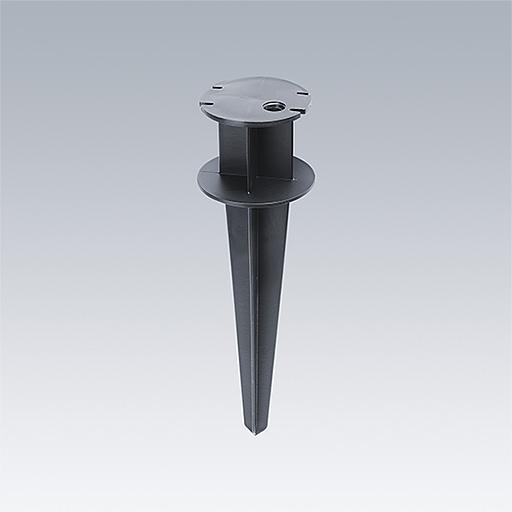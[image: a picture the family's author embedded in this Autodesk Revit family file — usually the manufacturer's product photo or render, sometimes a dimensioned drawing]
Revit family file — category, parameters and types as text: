
# Revit family: Thorn CESAR BOW
name_source: partatom
category: Lighting Fixtures
units: mm (PartAtom-declared; Revit-internal decimal feet)

## family parameters
Always vertical = No
Cut with Voids When Loaded = Yes
Light Source = Yes
Maintain Annotation Orientation = No
Part Type = Normal
Room Calculation Point = Yes
Round Connector Dimension = Use Diameter
Shared = No
Work Plane-Based = No

## types (96) — shared parameters
Assembly Code = Pr_70_70_48_62
Color Filter = 16777215
Description = Ground Surface Mounted Luminaire
Dimming Lamp Color Temperature Shift = <None>
Export Type to IFC As = IfcLightFixtureType
Ground Spike = No
Lamp = LED
Manufacturer = Thorn Lighting
Power Factor = 0.97
SELECT ACCESSORIES = SELECT ACCESSORIES
SELECT HOUSING = SELECT HOUSING
SELECT LIGHT DISTRIBUTION = SELECT LIGHT DISTRIBUTION
Tilt Angle = 90.00°
Type IFC Predefined Type = DIRECTIONSOURCE
URL = https://www.thornlighting.com
zero-valued in all types: Default Elevation, H

## per-type parameters (varying)
| type | Apparent Load | Beam Assymetric | Beam Medium | Beam Narrow | Beam Wide | Inner Circle Diameter | Inner Circle Radius | Luminaire Diameter | Luminaire Height | Luminaire Length | Luminaire Radius | Luminaire Width | Material Housing | Model | Photometric Web File | Size Medium | Size Small | Type Image |
| CESAR BOW S 4L 927 NB RD ANT | 8 VA | No | No | Yes | No | 46.5 mm  [stored 0.152559 ft] | 93 mm  [stored 0.305118 ft] | 100 mm  [stored 0.328084 ft] | 29 mm  [stored 0.0951444 ft] | 200 mm  [stored 0.656168 ft] | 200 mm  [stored 0.656168 ft] | 200 mm  [stored 0.656168 ft] | Thorn-Aluminium-RAL 7016-Anthracite Grey | 96800712 | 96800712_(STD).IES | No | Yes | TLG_CESA_F_BOW_S_ANT.jpg |
| CESAR BOW S 4L 927 NB RD BK | 8 VA | No | No | Yes | No | 46.5 mm  [stored 0.152559 ft] | 93 mm  [stored 0.305118 ft] | 100 mm  [stored 0.328084 ft] | 29 mm  [stored 0.0951444 ft] | 200 mm  [stored 0.656168 ft] | 200 mm  [stored 0.656168 ft] | 200 mm  [stored 0.656168 ft] | Thorn-Aluminium-RAL 9005-Jet Black | 96800710 | 96800710_(STD).IES | No | Yes | TLG_CESA_F_BOW_S_BK.jpg |
| CESAR BOW S 4L 927 NB RD GY | 8 VA | No | No | Yes | No | 46.5 mm  [stored 0.152559 ft] | 93 mm  [stored 0.305118 ft] | 100 mm  [stored 0.328084 ft] | 29 mm  [stored 0.0951444 ft] | 200 mm  [stored 0.656168 ft] | 200 mm  [stored 0.656168 ft] | 200 mm  [stored 0.656168 ft] | Thorn-Aluminium-RAL 9006-White Aluminium | 96800711 | 96800711_(STD).IES | No | Yes | TLG_CESA_F_BOW_S_GY.jpg |
| CESAR BOW S 4L 927 NB RD WH | 8 VA | No | No | Yes | No | 46.5 mm  [stored 0.152559 ft] | 93 mm  [stored 0.305118 ft] | 100 mm  [stored 0.328084 ft] | 29 mm  [stored 0.0951444 ft] | 200 mm  [stored 0.656168 ft] | 200 mm  [stored 0.656168 ft] | 200 mm  [stored 0.656168 ft] | Thorn-Aluminium-RAL 9016-Traffic White | 96800709 | 96800709_(STD).IES | No | Yes | TLG_CESA_F_BOW_S_WH.jpg |
| CESAR BOW S 4L 930 NB RD ANT | 8 VA | No | No | Yes | No | 46.5 mm  [stored 0.152559 ft] | 93 mm  [stored 0.305118 ft] | 100 mm  [stored 0.328084 ft] | 29 mm  [stored 0.0951444 ft] | 200 mm  [stored 0.656168 ft] | 200 mm  [stored 0.656168 ft] | 200 mm  [stored 0.656168 ft] | Thorn-Aluminium-RAL 7016-Anthracite Grey | 96800720 | 96800720_(STD).IES | No | Yes | TLG_CESA_F_BOW_S_ANT.jpg |
| CESAR BOW S 4L 930 NB RD BK | 8 VA | No | No | Yes | No | 46.5 mm  [stored 0.152559 ft] | 93 mm  [stored 0.305118 ft] | 100 mm  [stored 0.328084 ft] | 29 mm  [stored 0.0951444 ft] | 200 mm  [stored 0.656168 ft] | 200 mm  [stored 0.656168 ft] | 200 mm  [stored 0.656168 ft] | Thorn-Aluminium-RAL 9005-Jet Black | 96800718 | 96800718_(STD).IES | No | Yes | TLG_CESA_F_BOW_S_BK.jpg |
| CESAR BOW S 4L 930 NB RD GY | 8 VA | No | No | Yes | No | 46.5 mm  [stored 0.152559 ft] | 93 mm  [stored 0.305118 ft] | 100 mm  [stored 0.328084 ft] | 29 mm  [stored 0.0951444 ft] | 200 mm  [stored 0.656168 ft] | 200 mm  [stored 0.656168 ft] | 200 mm  [stored 0.656168 ft] | Thorn-Aluminium-RAL 9006-White Aluminium | 96800719 | 96800719_(STD).IES | No | Yes | TLG_CESA_F_BOW_S_GY.jpg |
| CESAR BOW S 4L 930 NB RD WH | 8 VA | No | No | Yes | No | 46.5 mm  [stored 0.152559 ft] | 93 mm  [stored 0.305118 ft] | 100 mm  [stored 0.328084 ft] | 29 mm  [stored 0.0951444 ft] | 200 mm  [stored 0.656168 ft] | 200 mm  [stored 0.656168 ft] | 200 mm  [stored 0.656168 ft] | Thorn-Aluminium-RAL 9016-Traffic White | 96800717 | 96800717_(STD).IES | No | Yes | TLG_CESA_F_BOW_S_WH.jpg |
| CESAR BOW S 4L 940 NB RD ANT | 8 VA | No | No | Yes | No | 46.5 mm  [stored 0.152559 ft] | 93 mm  [stored 0.305118 ft] | 100 mm  [stored 0.328084 ft] | 29 mm  [stored 0.0951444 ft] | 200 mm  [stored 0.656168 ft] | 200 mm  [stored 0.656168 ft] | 200 mm  [stored 0.656168 ft] | Thorn-Aluminium-RAL 7016-Anthracite Grey | 96800716 | 96800716_(STD).IES | No | Yes | TLG_CESA_F_BOW_S_ANT.jpg |
| CESAR BOW S 4L 940 NB RD BK | 8 VA | No | No | Yes | No | 46.5 mm  [stored 0.152559 ft] | 93 mm  [stored 0.305118 ft] | 100 mm  [stored 0.328084 ft] | 29 mm  [stored 0.0951444 ft] | 200 mm  [stored 0.656168 ft] | 200 mm  [stored 0.656168 ft] | 200 mm  [stored 0.656168 ft] | Thorn-Aluminium-RAL 9005-Jet Black | 96800714 | 96800714_(STD).IES | No | Yes | TLG_CESA_F_BOW_S_BK.jpg |
| CESAR BOW S 4L 940 NB RD GY | 8 VA | No | No | Yes | No | 46.5 mm  [stored 0.152559 ft] | 93 mm  [stored 0.305118 ft] | 100 mm  [stored 0.328084 ft] | 29 mm  [stored 0.0951444 ft] | 200 mm  [stored 0.656168 ft] | 200 mm  [stored 0.656168 ft] | 200 mm  [stored 0.656168 ft] | Thorn-Aluminium-RAL 9006-White Aluminium | 96800715 | 96800715_(STD).IES | No | Yes | TLG_CESA_F_BOW_S_GY.jpg |
| CESAR BOW S 4L 940 NB RD WH | 8 VA | No | No | Yes | No | 46.5 mm  [stored 0.152559 ft] | 93 mm  [stored 0.305118 ft] | 100 mm  [stored 0.328084 ft] | 29 mm  [stored 0.0951444 ft] | 200 mm  [stored 0.656168 ft] | 200 mm  [stored 0.656168 ft] | 200 mm  [stored 0.656168 ft] | Thorn-Aluminium-RAL 9016-Traffic White | 96800713 | 96800713_(STD).IES | No | Yes | TLG_CESA_F_BOW_S_WH.jpg |
| CESAR BOW S 4L 927 MB RD ANT | 8 VA | No | Yes | No | No | 46.5 mm  [stored 0.152559 ft] | 93 mm  [stored 0.305118 ft] | 100 mm  [stored 0.328084 ft] | 29 mm  [stored 0.0951444 ft] | 200 mm  [stored 0.656168 ft] | 200 mm  [stored 0.656168 ft] | 200 mm  [stored 0.656168 ft] | Thorn-Aluminium-RAL 7016-Anthracite Grey | 96800724 | 96800724_(STD).IES | No | Yes | TLG_CESA_F_BOW_S_ANT.jpg |
| CESAR BOW S 4L 927 MB RD BK | 8 VA | No | Yes | No | No | 46.5 mm  [stored 0.152559 ft] | 93 mm  [stored 0.305118 ft] | 100 mm  [stored 0.328084 ft] | 29 mm  [stored 0.0951444 ft] | 200 mm  [stored 0.656168 ft] | 200 mm  [stored 0.656168 ft] | 200 mm  [stored 0.656168 ft] | Thorn-Aluminium-RAL 9005-Jet Black | 96800722 | 96800722_(STD).IES | No | Yes | TLG_CESA_F_BOW_S_BK.jpg |
| CESAR BOW S 4L 927 MB RD GY | 8 VA | No | Yes | No | No | 46.5 mm  [stored 0.152559 ft] | 93 mm  [stored 0.305118 ft] | 100 mm  [stored 0.328084 ft] | 29 mm  [stored 0.0951444 ft] | 200 mm  [stored 0.656168 ft] | 200 mm  [stored 0.656168 ft] | 200 mm  [stored 0.656168 ft] | Thorn-Aluminium-RAL 9006-White Aluminium | 96800723 | 96800723_(STD).IES | No | Yes | TLG_CESA_F_BOW_S_GY.jpg |
| CESAR BOW S 4L 927 MB RD WH | 8 VA | No | Yes | No | No | 46.5 mm  [stored 0.152559 ft] | 93 mm  [stored 0.305118 ft] | 100 mm  [stored 0.328084 ft] | 29 mm  [stored 0.0951444 ft] | 200 mm  [stored 0.656168 ft] | 200 mm  [stored 0.656168 ft] | 200 mm  [stored 0.656168 ft] | Thorn-Aluminium-RAL 9016-Traffic White | 96800721 | 96800721_(STD).IES | No | Yes | TLG_CESA_F_BOW_S_WH.jpg |
| CESAR BOW S 4L 930 MB RD ANT | 8 VA | No | Yes | No | No | 46.5 mm  [stored 0.152559 ft] | 93 mm  [stored 0.305118 ft] | 100 mm  [stored 0.328084 ft] | 29 mm  [stored 0.0951444 ft] | 200 mm  [stored 0.656168 ft] | 200 mm  [stored 0.656168 ft] | 200 mm  [stored 0.656168 ft] | Thorn-Aluminium-RAL 7016-Anthracite Grey | 96800732 | 96800732_(STD).IES | No | Yes | TLG_CESA_F_BOW_S_ANT.jpg |
| CESAR BOW S 4L 930 MB RD BK | 8 VA | No | Yes | No | No | 46.5 mm  [stored 0.152559 ft] | 93 mm  [stored 0.305118 ft] | 100 mm  [stored 0.328084 ft] | 29 mm  [stored 0.0951444 ft] | 200 mm  [stored 0.656168 ft] | 200 mm  [stored 0.656168 ft] | 200 mm  [stored 0.656168 ft] | Thorn-Aluminium-RAL 9005-Jet Black | 96800730 | 96800730_(STD).IES | No | Yes | TLG_CESA_F_BOW_S_BK.jpg |
| CESAR BOW S 4L 930 MB RD GY | 8 VA | No | Yes | No | No | 46.5 mm  [stored 0.152559 ft] | 93 mm  [stored 0.305118 ft] | 100 mm  [stored 0.328084 ft] | 29 mm  [stored 0.0951444 ft] | 200 mm  [stored 0.656168 ft] | 200 mm  [stored 0.656168 ft] | 200 mm  [stored 0.656168 ft] | Thorn-Aluminium-RAL 9006-White Aluminium | 96800731 | 96800731_(STD).IES | No | Yes | TLG_CESA_F_BOW_S_GY.jpg |
| CESAR BOW S 4L 930 MB RD WH | 8 VA | No | Yes | No | No | 46.5 mm  [stored 0.152559 ft] | 93 mm  [stored 0.305118 ft] | 100 mm  [stored 0.328084 ft] | 29 mm  [stored 0.0951444 ft] | 200 mm  [stored 0.656168 ft] | 200 mm  [stored 0.656168 ft] | 200 mm  [stored 0.656168 ft] | Thorn-Aluminium-RAL 9016-Traffic White | 96800729 | 96800729_(STD).IES | No | Yes | TLG_CESA_F_BOW_S_WH.jpg |
| CESAR BOW S 4L 940 MB RD ANT | 8 VA | No | Yes | No | No | 46.5 mm  [stored 0.152559 ft] | 93 mm  [stored 0.305118 ft] | 100 mm  [stored 0.328084 ft] | 29 mm  [stored 0.0951444 ft] | 200 mm  [stored 0.656168 ft] | 200 mm  [stored 0.656168 ft] | 200 mm  [stored 0.656168 ft] | Thorn-Aluminium-RAL 7016-Anthracite Grey | 96800728 | 96800728_(STD).IES | No | Yes | TLG_CESA_F_BOW_S_ANT.jpg |
| CESAR BOW S 4L 940 MB RD BK | 8 VA | No | Yes | No | No | 46.5 mm  [stored 0.152559 ft] | 93 mm  [stored 0.305118 ft] | 100 mm  [stored 0.328084 ft] | 29 mm  [stored 0.0951444 ft] | 200 mm  [stored 0.656168 ft] | 200 mm  [stored 0.656168 ft] | 200 mm  [stored 0.656168 ft] | Thorn-Aluminium-RAL 9005-Jet Black | 96800726 | 96800726_(STD).IES | No | Yes | TLG_CESA_F_BOW_S_BK.jpg |
| CESAR BOW S 4L 940 MB RD GY | 8 VA | No | Yes | No | No | 46.5 mm  [stored 0.152559 ft] | 93 mm  [stored 0.305118 ft] | 100 mm  [stored 0.328084 ft] | 29 mm  [stored 0.0951444 ft] | 200 mm  [stored 0.656168 ft] | 200 mm  [stored 0.656168 ft] | 200 mm  [stored 0.656168 ft] | Thorn-Aluminium-RAL 9006-White Aluminium | 96800727 | 96800727_(STD).IES | No | Yes | TLG_CESA_F_BOW_S_GY.jpg |
| CESAR BOW S 4L 940 MB RD WH | 8 VA | No | Yes | No | No | 46.5 mm  [stored 0.152559 ft] | 93 mm  [stored 0.305118 ft] | 100 mm  [stored 0.328084 ft] | 29 mm  [stored 0.0951444 ft] | 200 mm  [stored 0.656168 ft] | 200 mm  [stored 0.656168 ft] | 200 mm  [stored 0.656168 ft] | Thorn-Aluminium-RAL 9016-Traffic White | 96800725 | 96800725_(STD).IES | No | Yes | TLG_CESA_F_BOW_S_WH.jpg |
| CESAR BOW S 4L 927 WB RD ANT | 8 VA | No | No | No | Yes | 46.5 mm  [stored 0.152559 ft] | 93 mm  [stored 0.305118 ft] | 100 mm  [stored 0.328084 ft] | 29 mm  [stored 0.0951444 ft] | 200 mm  [stored 0.656168 ft] | 200 mm  [stored 0.656168 ft] | 200 mm  [stored 0.656168 ft] | Thorn-Aluminium-RAL 7016-Anthracite Grey | 96800736 | 96800736_(STD).IES | No | Yes | TLG_CESA_F_BOW_S_ANT.jpg |
| CESAR BOW S 4L 927 WB RD BK | 8 VA | No | No | No | Yes | 46.5 mm  [stored 0.152559 ft] | 93 mm  [stored 0.305118 ft] | 100 mm  [stored 0.328084 ft] | 29 mm  [stored 0.0951444 ft] | 200 mm  [stored 0.656168 ft] | 200 mm  [stored 0.656168 ft] | 200 mm  [stored 0.656168 ft] | Thorn-Aluminium-RAL 9005-Jet Black | 96800734 | 96800734_(STD).IES | No | Yes | TLG_CESA_F_BOW_S_BK.jpg |
| CESAR BOW S 4L 927 WB RD GY | 8 VA | No | No | No | Yes | 46.5 mm  [stored 0.152559 ft] | 93 mm  [stored 0.305118 ft] | 100 mm  [stored 0.328084 ft] | 29 mm  [stored 0.0951444 ft] | 200 mm  [stored 0.656168 ft] | 200 mm  [stored 0.656168 ft] | 200 mm  [stored 0.656168 ft] | Thorn-Aluminium-RAL 9006-White Aluminium | 96800735 | 96800735_(STD).IES | No | Yes | TLG_CESA_F_BOW_S_GY.jpg |
| CESAR BOW S 4L 927 WB RD WH | 8 VA | No | No | No | Yes | 46.5 mm  [stored 0.152559 ft] | 93 mm  [stored 0.305118 ft] | 100 mm  [stored 0.328084 ft] | 29 mm  [stored 0.0951444 ft] | 200 mm  [stored 0.656168 ft] | 200 mm  [stored 0.656168 ft] | 200 mm  [stored 0.656168 ft] | Thorn-Aluminium-RAL 9016-Traffic White | 96800733 | 96800733_(STD).IES | No | Yes | TLG_CESA_F_BOW_S_WH.jpg |
| CESAR BOW S 4L 930 WB RD ANT | 8 VA | No | No | No | Yes | 46.5 mm  [stored 0.152559 ft] | 93 mm  [stored 0.305118 ft] | 100 mm  [stored 0.328084 ft] | 29 mm  [stored 0.0951444 ft] | 200 mm  [stored 0.656168 ft] | 200 mm  [stored 0.656168 ft] | 200 mm  [stored 0.656168 ft] | Thorn-Aluminium-RAL 7016-Anthracite Grey | 96800744 | 96800744_(STD).IES | No | Yes | TLG_CESA_F_BOW_S_ANT.jpg |
| CESAR BOW S 4L 930 WB RD BK | 8 VA | No | No | No | Yes | 46.5 mm  [stored 0.152559 ft] | 93 mm  [stored 0.305118 ft] | 100 mm  [stored 0.328084 ft] | 29 mm  [stored 0.0951444 ft] | 200 mm  [stored 0.656168 ft] | 200 mm  [stored 0.656168 ft] | 200 mm  [stored 0.656168 ft] | Thorn-Aluminium-RAL 9005-Jet Black | 96800742 | 96800742_(STD).IES | No | Yes | TLG_CESA_F_BOW_S_BK.jpg |
| CESAR BOW S 4L 930 WB RD GY | 8 VA | No | No | No | Yes | 46.5 mm  [stored 0.152559 ft] | 93 mm  [stored 0.305118 ft] | 100 mm  [stored 0.328084 ft] | 29 mm  [stored 0.0951444 ft] | 200 mm  [stored 0.656168 ft] | 200 mm  [stored 0.656168 ft] | 200 mm  [stored 0.656168 ft] | Thorn-Aluminium-RAL 9006-White Aluminium | 96800743 | 96800743_(STD).IES | No | Yes | TLG_CESA_F_BOW_S_GY.jpg |
| CESAR BOW S 4L 930 WB RD WH | 8 VA | No | No | No | Yes | 46.5 mm  [stored 0.152559 ft] | 93 mm  [stored 0.305118 ft] | 100 mm  [stored 0.328084 ft] | 29 mm  [stored 0.0951444 ft] | 200 mm  [stored 0.656168 ft] | 200 mm  [stored 0.656168 ft] | 200 mm  [stored 0.656168 ft] | Thorn-Aluminium-RAL 9016-Traffic White | 96800741 | 96800741_(STD).IES | No | Yes | TLG_CESA_F_BOW_S_WH.jpg |
| CESAR BOW S 4L 940 WB RD ANT | 8 VA | No | No | No | Yes | 46.5 mm  [stored 0.152559 ft] | 93 mm  [stored 0.305118 ft] | 100 mm  [stored 0.328084 ft] | 29 mm  [stored 0.0951444 ft] | 200 mm  [stored 0.656168 ft] | 200 mm  [stored 0.656168 ft] | 200 mm  [stored 0.656168 ft] | Thorn-Aluminium-RAL 7016-Anthracite Grey | 96800740 | 96800740_(STD).IES | No | Yes | TLG_CESA_F_BOW_S_ANT.jpg |
| CESAR BOW S 4L 940 WB RD BK | 8 VA | No | No | No | Yes | 46.5 mm  [stored 0.152559 ft] | 93 mm  [stored 0.305118 ft] | 100 mm  [stored 0.328084 ft] | 29 mm  [stored 0.0951444 ft] | 200 mm  [stored 0.656168 ft] | 200 mm  [stored 0.656168 ft] | 200 mm  [stored 0.656168 ft] | Thorn-Aluminium-RAL 9005-Jet Black | 96800738 | 96800738_(STD).IES | No | Yes | TLG_CESA_F_BOW_S_BK.jpg |
| CESAR BOW S 4L 940 WB RD GY | 8 VA | No | No | No | Yes | 46.5 mm  [stored 0.152559 ft] | 93 mm  [stored 0.305118 ft] | 100 mm  [stored 0.328084 ft] | 29 mm  [stored 0.0951444 ft] | 200 mm  [stored 0.656168 ft] | 200 mm  [stored 0.656168 ft] | 200 mm  [stored 0.656168 ft] | Thorn-Aluminium-RAL 9006-White Aluminium | 96800739 | 96800739_(STD).IES | No | Yes | TLG_CESA_F_BOW_S_GY.jpg |
| CESAR BOW S 4L 940 WB RD WH | 8 VA | No | No | No | Yes | 46.5 mm  [stored 0.152559 ft] | 93 mm  [stored 0.305118 ft] | 100 mm  [stored 0.328084 ft] | 29 mm  [stored 0.0951444 ft] | 200 mm  [stored 0.656168 ft] | 200 mm  [stored 0.656168 ft] | 200 mm  [stored 0.656168 ft] | Thorn-Aluminium-RAL 9016-Traffic White | 96800737 | 96800737_(STD).IES | No | Yes | TLG_CESA_F_BOW_S_WH.jpg |
| CESAR BOW S 4L 927 AS RD ANT | 8 VA | Yes | No | No | No | 46.5 mm  [stored 0.152559 ft] | 93 mm  [stored 0.305118 ft] | 100 mm  [stored 0.328084 ft] | 29 mm  [stored 0.0951444 ft] | 200 mm  [stored 0.656168 ft] | 200 mm  [stored 0.656168 ft] | 200 mm  [stored 0.656168 ft] | Thorn-Aluminium-RAL 7016-Anthracite Grey | 96800748 | 96800748_(STD).IES | No | Yes | TLG_CESA_F_BOW_S_ANT.jpg |
| CESAR BOW S 4L 927 AS RD BK | 8 VA | Yes | No | No | No | 46.5 mm  [stored 0.152559 ft] | 93 mm  [stored 0.305118 ft] | 100 mm  [stored 0.328084 ft] | 29 mm  [stored 0.0951444 ft] | 200 mm  [stored 0.656168 ft] | 200 mm  [stored 0.656168 ft] | 200 mm  [stored 0.656168 ft] | Thorn-Aluminium-RAL 9005-Jet Black | 96800746 | 96800746_(STD).IES | No | Yes | TLG_CESA_F_BOW_S_BK.jpg |
| CESAR BOW S 4L 927 AS RD GY | 8 VA | Yes | No | No | No | 46.5 mm  [stored 0.152559 ft] | 93 mm  [stored 0.305118 ft] | 100 mm  [stored 0.328084 ft] | 29 mm  [stored 0.0951444 ft] | 200 mm  [stored 0.656168 ft] | 200 mm  [stored 0.656168 ft] | 200 mm  [stored 0.656168 ft] | Thorn-Aluminium-RAL 9006-White Aluminium | 96800747 | 96800747_(STD).IES | No | Yes | TLG_CESA_F_BOW_S_GY.jpg |
| CESAR BOW S 4L 927 AS RD WH | 8 VA | Yes | No | No | No | 46.5 mm  [stored 0.152559 ft] | 93 mm  [stored 0.305118 ft] | 100 mm  [stored 0.328084 ft] | 29 mm  [stored 0.0951444 ft] | 200 mm  [stored 0.656168 ft] | 200 mm  [stored 0.656168 ft] | 200 mm  [stored 0.656168 ft] | Thorn-Aluminium-RAL 9016-Traffic White | 96800745 | 96800745_(STD).IES | No | Yes | TLG_CESA_F_BOW_S_WH.jpg |
| CESAR BOW S 4L 930 AS RD ANT | 8 VA | Yes | No | No | No | 46.5 mm  [stored 0.152559 ft] | 93 mm  [stored 0.305118 ft] | 100 mm  [stored 0.328084 ft] | 29 mm  [stored 0.0951444 ft] | 200 mm  [stored 0.656168 ft] | 200 mm  [stored 0.656168 ft] | 200 mm  [stored 0.656168 ft] | Thorn-Aluminium-RAL 7016-Anthracite Grey | 96800756 | 96800756_(STD).IES | No | Yes | TLG_CESA_F_BOW_S_ANT.jpg |
| CESAR BOW S 4L 930 AS RD BK | 8 VA | Yes | No | No | No | 46.5 mm  [stored 0.152559 ft] | 93 mm  [stored 0.305118 ft] | 100 mm  [stored 0.328084 ft] | 29 mm  [stored 0.0951444 ft] | 200 mm  [stored 0.656168 ft] | 200 mm  [stored 0.656168 ft] | 200 mm  [stored 0.656168 ft] | Thorn-Aluminium-RAL 9005-Jet Black | 96800754 | 96800754_(STD).IES | No | Yes | TLG_CESA_F_BOW_S_BK.jpg |
| CESAR BOW S 4L 930 AS RD GY | 8 VA | Yes | No | No | No | 46.5 mm  [stored 0.152559 ft] | 93 mm  [stored 0.305118 ft] | 100 mm  [stored 0.328084 ft] | 29 mm  [stored 0.0951444 ft] | 200 mm  [stored 0.656168 ft] | 200 mm  [stored 0.656168 ft] | 200 mm  [stored 0.656168 ft] | Thorn-Aluminium-RAL 9006-White Aluminium | 96800755 | 96800755_(STD).IES | No | Yes | TLG_CESA_F_BOW_S_GY.jpg |
| CESAR BOW S 4L 930 AS RD WH | 8 VA | Yes | No | No | No | 46.5 mm  [stored 0.152559 ft] | 93 mm  [stored 0.305118 ft] | 100 mm  [stored 0.328084 ft] | 29 mm  [stored 0.0951444 ft] | 200 mm  [stored 0.656168 ft] | 200 mm  [stored 0.656168 ft] | 200 mm  [stored 0.656168 ft] | Thorn-Aluminium-RAL 9016-Traffic White | 96800753 | 96800753_(STD).IES | No | Yes | TLG_CESA_F_BOW_S_WH.jpg |
| CESAR BOW S 4L 940 AS RD ANT | 8 VA | Yes | No | No | No | 46.5 mm  [stored 0.152559 ft] | 93 mm  [stored 0.305118 ft] | 100 mm  [stored 0.328084 ft] | 29 mm  [stored 0.0951444 ft] | 200 mm  [stored 0.656168 ft] | 200 mm  [stored 0.656168 ft] | 200 mm  [stored 0.656168 ft] | Thorn-Aluminium-RAL 7016-Anthracite Grey | 96800752 | 96800752_(STD).IES | No | Yes | TLG_CESA_F_BOW_S_ANT.jpg |
| CESAR BOW S 4L 940 AS RD BK | 8 VA | Yes | No | No | No | 46.5 mm  [stored 0.152559 ft] | 93 mm  [stored 0.305118 ft] | 100 mm  [stored 0.328084 ft] | 29 mm  [stored 0.0951444 ft] | 200 mm  [stored 0.656168 ft] | 200 mm  [stored 0.656168 ft] | 200 mm  [stored 0.656168 ft] | Thorn-Aluminium-RAL 9005-Jet Black | 96800750 | 96800750_(STD).IES | No | Yes | TLG_CESA_F_BOW_S_BK.jpg |
| CESAR BOW S 4L 940 AS RD GY | 8 VA | Yes | No | No | No | 46.5 mm  [stored 0.152559 ft] | 93 mm  [stored 0.305118 ft] | 100 mm  [stored 0.328084 ft] | 29 mm  [stored 0.0951444 ft] | 200 mm  [stored 0.656168 ft] | 200 mm  [stored 0.656168 ft] | 200 mm  [stored 0.656168 ft] | Thorn-Aluminium-RAL 9006-White Aluminium | 96800751 | 96800751_(STD).IES | No | Yes | TLG_CESA_F_BOW_S_GY.jpg |
| CESAR BOW S 4L 940 AS RD WH | 8 VA | Yes | No | No | No | 46.5 mm  [stored 0.152559 ft] | 93 mm  [stored 0.305118 ft] | 100 mm  [stored 0.328084 ft] | 29 mm  [stored 0.0951444 ft] | 200 mm  [stored 0.656168 ft] | 200 mm  [stored 0.656168 ft] | 200 mm  [stored 0.656168 ft] | Thorn-Aluminium-RAL 9016-Traffic White | 96800749 | 96800749_(STD).IES | No | Yes | TLG_CESA_F_BOW_S_WH.jpg |
| CESAR BOW M 9L 927 NB RD ANT | 19 VA | No | No | Yes | No | 69 mm  [stored 0.226378 ft] | 138 mm  [stored 0.452756 ft] | 130 mm  [stored 0.426509 ft] | 31 mm  [stored 0.101706 ft] | 260 mm  [stored 0.853018 ft] | 260 mm  [stored 0.853018 ft] | 260 mm  [stored 0.853018 ft] | Thorn-Aluminium-RAL 7016-Anthracite Grey | 96800760 | 96800760_(STD).IES | Yes | No | TLG_CESA_F_BOW_M_9L_ANT.jpg |
| CESAR BOW M 9L 927 NB RD BK | 19 VA | No | No | Yes | No | 69 mm  [stored 0.226378 ft] | 138 mm  [stored 0.452756 ft] | 130 mm  [stored 0.426509 ft] | 31 mm  [stored 0.101706 ft] | 260 mm  [stored 0.853018 ft] | 260 mm  [stored 0.853018 ft] | 260 mm  [stored 0.853018 ft] | Thorn-Aluminium-RAL 9005-Jet Black | 96800758 | 96800758_(STD).IES | Yes | No | TLG_CESA_F_BOW_M_9L_BK.jpg |
| CESAR BOW M 9L 927 NB RD GY | 19 VA | No | No | Yes | No | 69 mm  [stored 0.226378 ft] | 138 mm  [stored 0.452756 ft] | 130 mm  [stored 0.426509 ft] | 31 mm  [stored 0.101706 ft] | 260 mm  [stored 0.853018 ft] | 260 mm  [stored 0.853018 ft] | 260 mm  [stored 0.853018 ft] | Thorn-Aluminium-RAL 9006-White Aluminium | 96800759 | 96800759_(STD).IES | Yes | No | TLG_CESA_F_BOW_M_9L_GY.jpg |
| CESAR BOW M 9L 927 NB RD WH | 19 VA | No | No | Yes | No | 69 mm  [stored 0.226378 ft] | 138 mm  [stored 0.452756 ft] | 130 mm  [stored 0.426509 ft] | 31 mm  [stored 0.101706 ft] | 260 mm  [stored 0.853018 ft] | 260 mm  [stored 0.853018 ft] | 260 mm  [stored 0.853018 ft] | Thorn-Aluminium-RAL 9016-Traffic White | 96800757 | 96800757_(STD).IES | Yes | No | TLG_CESA_F_BOW_M_9L_WH.jpg |
| CESAR BOW M 9L 930 NB RD ANT | 19 VA | No | No | Yes | No | 69 mm  [stored 0.226378 ft] | 138 mm  [stored 0.452756 ft] | 130 mm  [stored 0.426509 ft] | 31 mm  [stored 0.101706 ft] | 260 mm  [stored 0.853018 ft] | 260 mm  [stored 0.853018 ft] | 260 mm  [stored 0.853018 ft] | Thorn-Aluminium-RAL 7016-Anthracite Grey | 96800768 | 96800768_(STD).IES | Yes | No | TLG_CESA_F_BOW_M_9L_ANT.jpg |
| CESAR BOW M 9L 930 NB RD BK | 19 VA | No | No | Yes | No | 69 mm  [stored 0.226378 ft] | 138 mm  [stored 0.452756 ft] | 130 mm  [stored 0.426509 ft] | 31 mm  [stored 0.101706 ft] | 260 mm  [stored 0.853018 ft] | 260 mm  [stored 0.853018 ft] | 260 mm  [stored 0.853018 ft] | Thorn-Aluminium-RAL 9005-Jet Black | 96800766 | 96800766_(STD).IES | Yes | No | TLG_CESA_F_BOW_M_9L_BK.jpg |
| CESAR BOW M 9L 930 NB RD GY | 19 VA | No | No | Yes | No | 69 mm  [stored 0.226378 ft] | 138 mm  [stored 0.452756 ft] | 130 mm  [stored 0.426509 ft] | 31 mm  [stored 0.101706 ft] | 260 mm  [stored 0.853018 ft] | 260 mm  [stored 0.853018 ft] | 260 mm  [stored 0.853018 ft] | Thorn-Aluminium-RAL 9006-White Aluminium | 96800767 | 96800767_(STD).IES | Yes | No | TLG_CESA_F_BOW_M_9L_GY.jpg |
| CESAR BOW M 9L 930 NB RD WH | 19 VA | No | No | Yes | No | 69 mm  [stored 0.226378 ft] | 138 mm  [stored 0.452756 ft] | 130 mm  [stored 0.426509 ft] | 31 mm  [stored 0.101706 ft] | 260 mm  [stored 0.853018 ft] | 260 mm  [stored 0.853018 ft] | 260 mm  [stored 0.853018 ft] | Thorn-Aluminium-RAL 9016-Traffic White | 96800765 | 96800765_(STD).IES | Yes | No | TLG_CESA_F_BOW_M_9L_WH.jpg |
| CESAR BOW M 9L 940 NB RD ANT | 19 VA | No | No | Yes | No | 69 mm  [stored 0.226378 ft] | 138 mm  [stored 0.452756 ft] | 130 mm  [stored 0.426509 ft] | 31 mm  [stored 0.101706 ft] | 260 mm  [stored 0.853018 ft] | 260 mm  [stored 0.853018 ft] | 260 mm  [stored 0.853018 ft] | Thorn-Aluminium-RAL 7016-Anthracite Grey | 96800764 | 96800764_(STD).IES | Yes | No | TLG_CESA_F_BOW_M_9L_ANT.jpg |
| CESAR BOW M 9L 940 NB RD BK | 19 VA | No | No | Yes | No | 69 mm  [stored 0.226378 ft] | 138 mm  [stored 0.452756 ft] | 130 mm  [stored 0.426509 ft] | 31 mm  [stored 0.101706 ft] | 260 mm  [stored 0.853018 ft] | 260 mm  [stored 0.853018 ft] | 260 mm  [stored 0.853018 ft] | Thorn-Aluminium-RAL 9005-Jet Black | 96800762 | 96800762_(STD).IES | Yes | No | TLG_CESA_F_BOW_M_9L_BK.jpg |
| CESAR BOW M 9L 940 NB RD GY | 19 VA | No | No | Yes | No | 69 mm  [stored 0.226378 ft] | 138 mm  [stored 0.452756 ft] | 130 mm  [stored 0.426509 ft] | 31 mm  [stored 0.101706 ft] | 260 mm  [stored 0.853018 ft] | 260 mm  [stored 0.853018 ft] | 260 mm  [stored 0.853018 ft] | Thorn-Aluminium-RAL 9006-White Aluminium | 96800763 | 96800763_(STD).IES | Yes | No | TLG_CESA_F_BOW_M_9L_GY.jpg |
| CESAR BOW M 9L 940 NB RD WH | 19 VA | No | No | Yes | No | 69 mm  [stored 0.226378 ft] | 138 mm  [stored 0.452756 ft] | 130 mm  [stored 0.426509 ft] | 31 mm  [stored 0.101706 ft] | 260 mm  [stored 0.853018 ft] | 260 mm  [stored 0.853018 ft] | 260 mm  [stored 0.853018 ft] | Thorn-Aluminium-RAL 9016-Traffic White | 96800761 | 96800761_(STD).IES | Yes | No | TLG_CESA_F_BOW_M_9L_WH.jpg |
| CESAR BOW M 9L 927 MB RD ANT | 19 VA | No | Yes | No | No | 69 mm  [stored 0.226378 ft] | 138 mm  [stored 0.452756 ft] | 130 mm  [stored 0.426509 ft] | 31 mm  [stored 0.101706 ft] | 260 mm  [stored 0.853018 ft] | 260 mm  [stored 0.853018 ft] | 260 mm  [stored 0.853018 ft] | Thorn-Aluminium-RAL 7016-Anthracite Grey | 96800772 | 96800772_(STD).IES | Yes | No | TLG_CESA_F_BOW_M_9L_ANT.jpg |
| CESAR BOW M 9L 927 MB RD BK | 19 VA | No | Yes | No | No | 69 mm  [stored 0.226378 ft] | 138 mm  [stored 0.452756 ft] | 130 mm  [stored 0.426509 ft] | 31 mm  [stored 0.101706 ft] | 260 mm  [stored 0.853018 ft] | 260 mm  [stored 0.853018 ft] | 260 mm  [stored 0.853018 ft] | Thorn-Aluminium-RAL 9005-Jet Black | 96800770 | 96800770_(STD).IES | Yes | No | TLG_CESA_F_BOW_M_9L_BK.jpg |
| CESAR BOW M 9L 927 MB RD GY | 19 VA | No | Yes | No | No | 69 mm  [stored 0.226378 ft] | 138 mm  [stored 0.452756 ft] | 130 mm  [stored 0.426509 ft] | 31 mm  [stored 0.101706 ft] | 260 mm  [stored 0.853018 ft] | 260 mm  [stored 0.853018 ft] | 260 mm  [stored 0.853018 ft] | Thorn-Aluminium-RAL 9006-White Aluminium | 96800771 | 96800771_(STD).IES | Yes | No | TLG_CESA_F_BOW_M_9L_GY.jpg |
| CESAR BOW M 9L 927 MB RD WH | 19 VA | No | Yes | No | No | 69 mm  [stored 0.226378 ft] | 138 mm  [stored 0.452756 ft] | 130 mm  [stored 0.426509 ft] | 31 mm  [stored 0.101706 ft] | 260 mm  [stored 0.853018 ft] | 260 mm  [stored 0.853018 ft] | 260 mm  [stored 0.853018 ft] | Thorn-Aluminium-RAL 9016-Traffic White | 96800769 | 96800769_(STD).IES | Yes | No | TLG_CESA_F_BOW_M_9L_WH.jpg |
| CESAR BOW M 9L 930 MB RD ANT | 19 VA | No | Yes | No | No | 69 mm  [stored 0.226378 ft] | 138 mm  [stored 0.452756 ft] | 130 mm  [stored 0.426509 ft] | 31 mm  [stored 0.101706 ft] | 260 mm  [stored 0.853018 ft] | 260 mm  [stored 0.853018 ft] | 260 mm  [stored 0.853018 ft] | Thorn-Aluminium-RAL 7016-Anthracite Grey | 96800780 | 96800780_(STD).IES | Yes | No | TLG_CESA_F_BOW_M_9L_ANT.jpg |
| CESAR BOW M 9L 930 MB RD BK | 19 VA | No | Yes | No | No | 69 mm  [stored 0.226378 ft] | 138 mm  [stored 0.452756 ft] | 130 mm  [stored 0.426509 ft] | 31 mm  [stored 0.101706 ft] | 260 mm  [stored 0.853018 ft] | 260 mm  [stored 0.853018 ft] | 260 mm  [stored 0.853018 ft] | Thorn-Aluminium-RAL 9005-Jet Black | 96800778 | 96800778_(STD).IES | Yes | No | TLG_CESA_F_BOW_M_9L_BK.jpg |
| CESAR BOW M 9L 930 MB RD GY | 19 VA | No | Yes | No | No | 69 mm  [stored 0.226378 ft] | 138 mm  [stored 0.452756 ft] | 130 mm  [stored 0.426509 ft] | 31 mm  [stored 0.101706 ft] | 260 mm  [stored 0.853018 ft] | 260 mm  [stored 0.853018 ft] | 260 mm  [stored 0.853018 ft] | Thorn-Aluminium-RAL 9006-White Aluminium | 96800779 | 96800779_(STD).IES | Yes | No | TLG_CESA_F_BOW_M_9L_GY.jpg |
| CESAR BOW M 9L 930 MB RD WH | 19 VA | No | Yes | No | No | 69 mm  [stored 0.226378 ft] | 138 mm  [stored 0.452756 ft] | 130 mm  [stored 0.426509 ft] | 31 mm  [stored 0.101706 ft] | 260 mm  [stored 0.853018 ft] | 260 mm  [stored 0.853018 ft] | 260 mm  [stored 0.853018 ft] | Thorn-Aluminium-RAL 9016-Traffic White | 96800777 | 96800777_(STD).IES | Yes | No | TLG_CESA_F_BOW_M_9L_WH.jpg |
| CESAR BOW M 9L 940 MB RD ANT | 19 VA | No | Yes | No | No | 69 mm  [stored 0.226378 ft] | 138 mm  [stored 0.452756 ft] | 130 mm  [stored 0.426509 ft] | 31 mm  [stored 0.101706 ft] | 260 mm  [stored 0.853018 ft] | 260 mm  [stored 0.853018 ft] | 260 mm  [stored 0.853018 ft] | Thorn-Aluminium-RAL 7016-Anthracite Grey | 96800776 | 96800776_(STD).IES | Yes | No | TLG_CESA_F_BOW_M_9L_ANT.jpg |
| CESAR BOW M 9L 940 MB RD BK | 19 VA | No | Yes | No | No | 69 mm  [stored 0.226378 ft] | 138 mm  [stored 0.452756 ft] | 130 mm  [stored 0.426509 ft] | 31 mm  [stored 0.101706 ft] | 260 mm  [stored 0.853018 ft] | 260 mm  [stored 0.853018 ft] | 260 mm  [stored 0.853018 ft] | Thorn-Aluminium-RAL 9005-Jet Black | 96800774 | 96800774_(STD).IES | Yes | No | TLG_CESA_F_BOW_M_9L_BK.jpg |
| CESAR BOW M 9L 940 MB RD GY | 19 VA | No | Yes | No | No | 69 mm  [stored 0.226378 ft] | 138 mm  [stored 0.452756 ft] | 130 mm  [stored 0.426509 ft] | 31 mm  [stored 0.101706 ft] | 260 mm  [stored 0.853018 ft] | 260 mm  [stored 0.853018 ft] | 260 mm  [stored 0.853018 ft] | Thorn-Aluminium-RAL 9006-White Aluminium | 96800775 | 96800775_(STD).IES | Yes | No | TLG_CESA_F_BOW_M_9L_GY.jpg |
| CESAR BOW M 9L 940 MB RD WH | 19 VA | No | Yes | No | No | 69 mm  [stored 0.226378 ft] | 138 mm  [stored 0.452756 ft] | 130 mm  [stored 0.426509 ft] | 31 mm  [stored 0.101706 ft] | 260 mm  [stored 0.853018 ft] | 260 mm  [stored 0.853018 ft] | 260 mm  [stored 0.853018 ft] | Thorn-Aluminium-RAL 9016-Traffic White | 96800773 | 96800773_(STD).IES | Yes | No | TLG_CESA_F_BOW_M_9L_WH.jpg |
| CESAR BOW M 9L 927 WB RD ANT | 19 VA | No | No | No | Yes | 69 mm  [stored 0.226378 ft] | 138 mm  [stored 0.452756 ft] | 130 mm  [stored 0.426509 ft] | 31 mm  [stored 0.101706 ft] | 260 mm  [stored 0.853018 ft] | 260 mm  [stored 0.853018 ft] | 260 mm  [stored 0.853018 ft] | Thorn-Aluminium-RAL 7016-Anthracite Grey | 96800784 | 96800784_(STD).IES | Yes | No | TLG_CESA_F_BOW_M_9L_ANT.jpg |
| CESAR BOW M 9L 927 WB RD BK | 19 VA | No | No | No | Yes | 69 mm  [stored 0.226378 ft] | 138 mm  [stored 0.452756 ft] | 130 mm  [stored 0.426509 ft] | 31 mm  [stored 0.101706 ft] | 260 mm  [stored 0.853018 ft] | 260 mm  [stored 0.853018 ft] | 260 mm  [stored 0.853018 ft] | Thorn-Aluminium-RAL 9005-Jet Black | 96800782 | 96800782_(STD).IES | Yes | No | TLG_CESA_F_BOW_M_9L_BK.jpg |
| CESAR BOW M 9L 927 WB RD GY | 19 VA | No | No | No | Yes | 69 mm  [stored 0.226378 ft] | 138 mm  [stored 0.452756 ft] | 130 mm  [stored 0.426509 ft] | 31 mm  [stored 0.101706 ft] | 260 mm  [stored 0.853018 ft] | 260 mm  [stored 0.853018 ft] | 260 mm  [stored 0.853018 ft] | Thorn-Aluminium-RAL 9006-White Aluminium | 96800783 | 96800783_(STD).IES | Yes | No | TLG_CESA_F_BOW_M_9L_GY.jpg |
| CESAR BOW M 9L 927 WB RD WH | 19 VA | No | No | No | Yes | 69 mm  [stored 0.226378 ft] | 138 mm  [stored 0.452756 ft] | 130 mm  [stored 0.426509 ft] | 31 mm  [stored 0.101706 ft] | 260 mm  [stored 0.853018 ft] | 260 mm  [stored 0.853018 ft] | 260 mm  [stored 0.853018 ft] | Thorn-Aluminium-RAL 9016-Traffic White | 96800781 | 96800781_(STD).IES | Yes | No | TLG_CESA_F_BOW_M_9L_WH.jpg |
| CESAR BOW M 9L 930 WB RD ANT | 19 VA | No | No | No | Yes | 69 mm  [stored 0.226378 ft] | 138 mm  [stored 0.452756 ft] | 130 mm  [stored 0.426509 ft] | 31 mm  [stored 0.101706 ft] | 260 mm  [stored 0.853018 ft] | 260 mm  [stored 0.853018 ft] | 260 mm  [stored 0.853018 ft] | Thorn-Aluminium-RAL 7016-Anthracite Grey | 96800792 | 96800792_(STD).IES | Yes | No | TLG_CESA_F_BOW_M_9L_ANT.jpg |
| CESAR BOW M 9L 930 WB RD BK | 19 VA | No | No | No | Yes | 69 mm  [stored 0.226378 ft] | 138 mm  [stored 0.452756 ft] | 130 mm  [stored 0.426509 ft] | 31 mm  [stored 0.101706 ft] | 260 mm  [stored 0.853018 ft] | 260 mm  [stored 0.853018 ft] | 260 mm  [stored 0.853018 ft] | Thorn-Aluminium-RAL 9005-Jet Black | 96800790 | 96800790_(STD).IES | Yes | No | TLG_CESA_F_BOW_M_9L_BK.jpg |
| CESAR BOW M 9L 930 WB RD GY | 19 VA | No | No | No | Yes | 69 mm  [stored 0.226378 ft] | 138 mm  [stored 0.452756 ft] | 130 mm  [stored 0.426509 ft] | 31 mm  [stored 0.101706 ft] | 260 mm  [stored 0.853018 ft] | 260 mm  [stored 0.853018 ft] | 260 mm  [stored 0.853018 ft] | Thorn-Aluminium-RAL 9006-White Aluminium | 96800791 | 96800791_(STD).IES | Yes | No | TLG_CESA_F_BOW_M_9L_GY.jpg |
| CESAR BOW M 9L 930 WB RD WH | 19 VA | No | No | No | Yes | 69 mm  [stored 0.226378 ft] | 138 mm  [stored 0.452756 ft] | 130 mm  [stored 0.426509 ft] | 31 mm  [stored 0.101706 ft] | 260 mm  [stored 0.853018 ft] | 260 mm  [stored 0.853018 ft] | 260 mm  [stored 0.853018 ft] | Thorn-Aluminium-RAL 9016-Traffic White | 96800789 | 96800789_(STD).IES | Yes | No | TLG_CESA_F_BOW_M_9L_WH.jpg |
| CESAR BOW M 9L 940 WB RD ANT | 19 VA | No | No | No | Yes | 69 mm  [stored 0.226378 ft] | 138 mm  [stored 0.452756 ft] | 130 mm  [stored 0.426509 ft] | 31 mm  [stored 0.101706 ft] | 260 mm  [stored 0.853018 ft] | 260 mm  [stored 0.853018 ft] | 260 mm  [stored 0.853018 ft] | Thorn-Aluminium-RAL 7016-Anthracite Grey | 96800788 | 96800788_(STD).IES | Yes | No | TLG_CESA_F_BOW_M_9L_ANT.jpg |
| CESAR BOW M 9L 940 WB RD BK | 19 VA | No | No | No | Yes | 69 mm  [stored 0.226378 ft] | 138 mm  [stored 0.452756 ft] | 130 mm  [stored 0.426509 ft] | 31 mm  [stored 0.101706 ft] | 260 mm  [stored 0.853018 ft] | 260 mm  [stored 0.853018 ft] | 260 mm  [stored 0.853018 ft] | Thorn-Aluminium-RAL 9005-Jet Black | 96800786 | 96800786_(STD).IES | Yes | No | TLG_CESA_F_BOW_M_9L_BK.jpg |
| CESAR BOW M 9L 940 WB RD GY | 19 VA | No | No | No | Yes | 69 mm  [stored 0.226378 ft] | 138 mm  [stored 0.452756 ft] | 130 mm  [stored 0.426509 ft] | 31 mm  [stored 0.101706 ft] | 260 mm  [stored 0.853018 ft] | 260 mm  [stored 0.853018 ft] | 260 mm  [stored 0.853018 ft] | Thorn-Aluminium-RAL 9006-White Aluminium | 96800787 | 96800787_(STD).IES | Yes | No | TLG_CESA_F_BOW_M_9L_GY.jpg |
| CESAR BOW M 9L 940 WB RD WH | 19 VA | No | No | No | Yes | 69 mm  [stored 0.226378 ft] | 138 mm  [stored 0.452756 ft] | 130 mm  [stored 0.426509 ft] | 31 mm  [stored 0.101706 ft] | 260 mm  [stored 0.853018 ft] | 260 mm  [stored 0.853018 ft] | 260 mm  [stored 0.853018 ft] | Thorn-Aluminium-RAL 9016-Traffic White | 96800785 | 96800785_(STD).IES | Yes | No | TLG_CESA_F_BOW_M_9L_WH.jpg |
| CESAR BOW M 9L 927 AS RD ANT | 19 VA | Yes | No | No | No | 69 mm  [stored 0.226378 ft] | 138 mm  [stored 0.452756 ft] | 130 mm  [stored 0.426509 ft] | 31 mm  [stored 0.101706 ft] | 260 mm  [stored 0.853018 ft] | 260 mm  [stored 0.853018 ft] | 260 mm  [stored 0.853018 ft] | Thorn-Aluminium-RAL 7016-Anthracite Grey | 96800796 | 96800796_(STD).IES | Yes | No | TLG_CESA_F_BOW_M_9L_ANT.jpg |
| CESAR BOW M 9L 927 AS RD BK | 19 VA | Yes | No | No | No | 69 mm  [stored 0.226378 ft] | 138 mm  [stored 0.452756 ft] | 130 mm  [stored 0.426509 ft] | 31 mm  [stored 0.101706 ft] | 260 mm  [stored 0.853018 ft] | 260 mm  [stored 0.853018 ft] | 260 mm  [stored 0.853018 ft] | Thorn-Aluminium-RAL 9005-Jet Black | 96800794 | 96800794_(STD).IES | Yes | No | TLG_CESA_F_BOW_M_9L_BK.jpg |
| CESAR BOW M 9L 927 AS RD GY | 19 VA | Yes | No | No | No | 69 mm  [stored 0.226378 ft] | 138 mm  [stored 0.452756 ft] | 130 mm  [stored 0.426509 ft] | 31 mm  [stored 0.101706 ft] | 260 mm  [stored 0.853018 ft] | 260 mm  [stored 0.853018 ft] | 260 mm  [stored 0.853018 ft] | Thorn-Aluminium-RAL 9006-White Aluminium | 96800795 | 96800795_(STD).IES | Yes | No | TLG_CESA_F_BOW_M_9L_GY.jpg |
| CESAR BOW M 9L 927 AS RD WH | 19 VA | Yes | No | No | No | 69 mm  [stored 0.226378 ft] | 138 mm  [stored 0.452756 ft] | 130 mm  [stored 0.426509 ft] | 31 mm  [stored 0.101706 ft] | 260 mm  [stored 0.853018 ft] | 260 mm  [stored 0.853018 ft] | 260 mm  [stored 0.853018 ft] | Thorn-Aluminium-RAL 9016-Traffic White | 96800793 | 96800793_(STD).IES | Yes | No | TLG_CESA_F_BOW_M_9L_WH.jpg |
| CESAR BOW M 9L 930 AS RD ANT | 19 VA | Yes | No | No | No | 69 mm  [stored 0.226378 ft] | 138 mm  [stored 0.452756 ft] | 130 mm  [stored 0.426509 ft] | 31 mm  [stored 0.101706 ft] | 260 mm  [stored 0.853018 ft] | 260 mm  [stored 0.853018 ft] | 260 mm  [stored 0.853018 ft] | Thorn-Aluminium-RAL 7016-Anthracite Grey | 96800804 | 96800804_(STD).IES | Yes | No | TLG_CESA_F_BOW_M_9L_ANT.jpg |
| CESAR BOW M 9L 930 AS RD BK | 19 VA | Yes | No | No | No | 69 mm  [stored 0.226378 ft] | 138 mm  [stored 0.452756 ft] | 130 mm  [stored 0.426509 ft] | 31 mm  [stored 0.101706 ft] | 260 mm  [stored 0.853018 ft] | 260 mm  [stored 0.853018 ft] | 260 mm  [stored 0.853018 ft] | Thorn-Aluminium-RAL 9005-Jet Black | 96800802 | 96800802_(STD).IES | Yes | No | TLG_CESA_F_BOW_M_9L_BK.jpg |
| CESAR BOW M 9L 930 AS RD GY | 19 VA | Yes | No | No | No | 69 mm  [stored 0.226378 ft] | 138 mm  [stored 0.452756 ft] | 130 mm  [stored 0.426509 ft] | 31 mm  [stored 0.101706 ft] | 260 mm  [stored 0.853018 ft] | 260 mm  [stored 0.853018 ft] | 260 mm  [stored 0.853018 ft] | Thorn-Aluminium-RAL 9006-White Aluminium | 96800803 | 96800803_(STD).IES | Yes | No | TLG_CESA_F_BOW_M_9L_GY.jpg |
| CESAR BOW M 9L 930 AS RD WH | 19 VA | Yes | No | No | No | 69 mm  [stored 0.226378 ft] | 138 mm  [stored 0.452756 ft] | 130 mm  [stored 0.426509 ft] | 31 mm  [stored 0.101706 ft] | 260 mm  [stored 0.853018 ft] | 260 mm  [stored 0.853018 ft] | 260 mm  [stored 0.853018 ft] | Thorn-Aluminium-RAL 9016-Traffic White | 96800801 | 96800801_(STD).IES | Yes | No | TLG_CESA_F_BOW_M_9L_WH.jpg |
| CESAR BOW M 9L 940 AS RD ANT | 19 VA | Yes | No | No | No | 69 mm  [stored 0.226378 ft] | 138 mm  [stored 0.452756 ft] | 130 mm  [stored 0.426509 ft] | 31 mm  [stored 0.101706 ft] | 260 mm  [stored 0.853018 ft] | 260 mm  [stored 0.853018 ft] | 260 mm  [stored 0.853018 ft] | Thorn-Aluminium-RAL 7016-Anthracite Grey | 96800800 | 96800800_(STD).IES | Yes | No | TLG_CESA_F_BOW_M_9L_ANT.jpg |
| CESAR BOW M 9L 940 AS RD BK | 19 VA | Yes | No | No | No | 69 mm  [stored 0.226378 ft] | 138 mm  [stored 0.452756 ft] | 130 mm  [stored 0.426509 ft] | 31 mm  [stored 0.101706 ft] | 260 mm  [stored 0.853018 ft] | 260 mm  [stored 0.853018 ft] | 260 mm  [stored 0.853018 ft] | Thorn-Aluminium-RAL 9005-Jet Black | 96800798 | 96800798_(STD).IES | Yes | No | TLG_CESA_F_BOW_M_9L_BK.jpg |
| CESAR BOW M 9L 940 AS RD GY | 19 VA | Yes | No | No | No | 69 mm  [stored 0.226378 ft] | 138 mm  [stored 0.452756 ft] | 130 mm  [stored 0.426509 ft] | 31 mm  [stored 0.101706 ft] | 260 mm  [stored 0.853018 ft] | 260 mm  [stored 0.853018 ft] | 260 mm  [stored 0.853018 ft] | Thorn-Aluminium-RAL 9006-White Aluminium | 96800799 | 96800799_(STD).IES | Yes | No | TLG_CESA_F_BOW_M_9L_GY.jpg |
| CESAR BOW M 9L 940 AS RD WH | 19 VA | Yes | No | No | No | 69 mm  [stored 0.226378 ft] | 138 mm  [stored 0.452756 ft] | 130 mm  [stored 0.426509 ft] | 31 mm  [stored 0.101706 ft] | 260 mm  [stored 0.853018 ft] | 260 mm  [stored 0.853018 ft] | 260 mm  [stored 0.853018 ft] | Thorn-Aluminium-RAL 9016-Traffic White | 96800797 | 96800797_(STD).IES | Yes | No | TLG_CESA_F_BOW_M_9L_WH.jpg |

note: [stored X ft] marks values corroborated as IEEE doubles in the binary element streams (Revit-internal decimal feet)

## geometry (parser evidence)
native form markers: Sweep x4
no freeform markers — native parametric forms only
